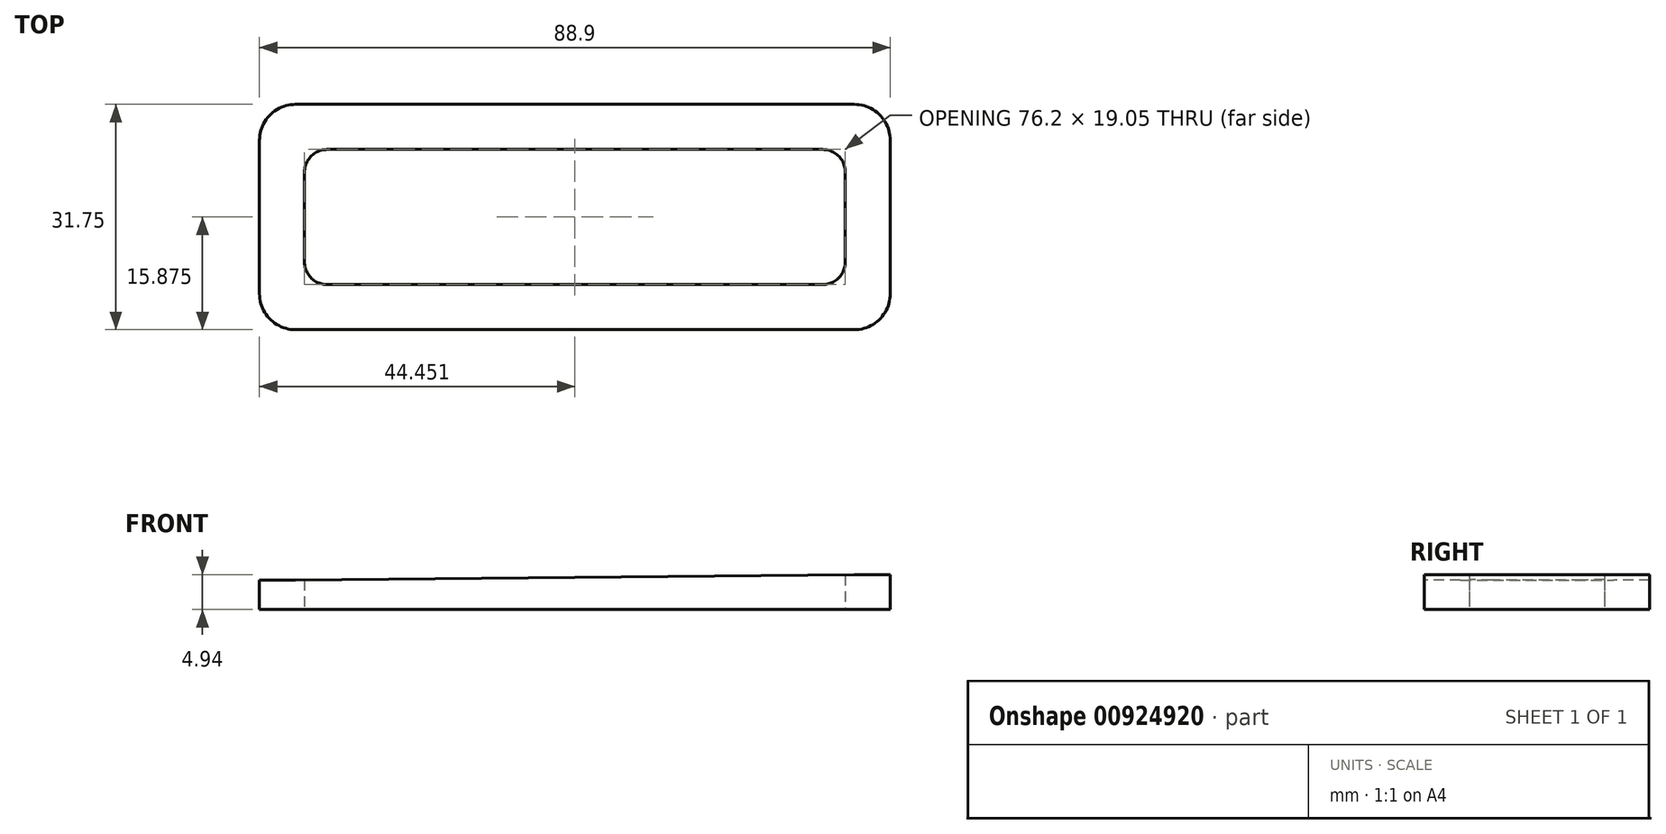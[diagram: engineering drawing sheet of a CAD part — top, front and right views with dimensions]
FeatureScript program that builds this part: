
annotation { "Feature Type Name" : "Feature", "Feature Type Description" : "" }
export const myFeature = defineFeature(function(context is Context, id is Id, definition is map)
    precondition{}
    {
        {
            var Q0;
            Q0=qCreatedBy(makeId("Front.planeOp"),FACE);
            var sketch = newSketch(context, id + "F0", { "sketchPlane" : qUnion([Q0])});
            skLineSegment(sketch, "E0", {"start": v(0, 0) * mm, "end": v(0, 2.39) * mm});
            skLineSegment(sketch, "E1", {"start": v(0, 2.39) * mm, "end": v(609.6, 7.95) * mm});
            skLineSegment(sketch, "E2", {"start": v(609.6, 7.95) * mm, "end": v(609.6, 0) * mm});
            skLineSegment(sketch, "E3", {"start": v(609.6, 0) * mm, "end": v(0, 0) * mm});
            skSolve(sketch);
        }
        {
            var Q0;
            Q0=qCreatedBy(makeId("Front.planeOp"),FACE);
            var sketch = newSketch(context, id + "F1", { "sketchPlane" : qUnion([Q0])});
            skLineSegment(sketch, "E4", {"start": v(609.6, 7.95) * mm, "end": v(520.7, 7.14) * mm});
            skLineSegment(sketch, "E5", {"start": v(520.7, 7.14) * mm, "end": v(520.7, 0) * mm});
            skLineSegment(sketch, "E6", {"start": v(520.7, 0) * mm, "end": v(609.6, 0) * mm});
            skLineSegment(sketch, "E7", {"start": v(609.6, 0) * mm, "end": v(609.6, 7.95) * mm});
            skSolve(sketch);
        }
        {
            var Q0;
            Q0=qCreatedBy(makeId("Front.planeOp"),FACE);
            var sketch = newSketch(context, id + "F2", { "sketchPlane" : qUnion([Q0])});
            skLineSegment(sketch, "E8", {"start": v(444.5, 6.44) * mm, "end": v(444.5, 0) * mm});
            skLineSegment(sketch, "E9", {"start": v(444.5, 0) * mm, "end": v(355.6, 0) * mm});
            skLineSegment(sketch, "E10", {"start": v(-261.65, 0) * mm, "end": v(-261.65, 0) * mm});
            skLineSegment(sketch, "E11", {"start": v(355.55, 5.63) * mm, "end": v(444.5, 6.44) * mm});
            skLineSegment(sketch, "E12", {"start": v(355.55, 5.63) * mm, "end": v(355.6, 0) * mm});
            skSolve(sketch);
        }
        {
            var Q0;
            Q0=makeQuery(id+"F0.imprint","IMPRINT",FACE,{"disambiguationData":[TD([[makeQuery(id+"F0.imprint","IMPRINT",EDGE,{"derivedFrom":sQuery(id+"F0.wireOp",EDGE,"E0")}),-1.0]])]});
            var sketch = newSketch(context, id + "F3", { "sketchPlane" : qUnion([Q0])});
            skLineSegment(sketch, "E13", {"start": v(279.35, 4.94) * mm, "end": v(279.35, 0) * mm});
            skLineSegment(sketch, "E14", {"start": v(279.35, 0) * mm, "end": v(190.45, 0) * mm});
            skLineSegment(sketch, "E15", {"start": v(190.45, 0) * mm, "end": v(190.45, 4.13) * mm});
            skLineSegment(sketch, "E16", {"start": v(190.45, 4.13) * mm, "end": v(279.35, 4.94) * mm});
            skSolve(sketch);
        }
        {
            var Q0;
            Q0=qSketchRegion(id+"F3",true);
            extrude(context, id + "F4", {"entities" : qUnion([Q0]), "depth" : 31.75 * mm, "offsetDistance" : 25.4 * mm});
        }
        {
            var Q0;
            Q0=makeQuery(id+"F4.opExtrude","SWEPT_FACE",FACE,{"disambiguationData":[OSD([sQuery(id+"F3.wireOp",EDGE,"E14")])]});
            var sketch = newSketch(context, id + "F5", { "sketchPlane" : qUnion([Q0])});
            skLineSegment(sketch, "E17.bottom", {"start": v(199.98, 25.4) * mm, "end": v(269.82, 25.4) * mm});
            skLineSegment(sketch, "E17.top", {"start": v(199.98, 6.35) * mm, "end": v(269.82, 6.35) * mm});
            skLineSegment(sketch, "E17.left", {"start": v(196.8, 22.22) * mm, "end": v(196.8, 9.52) * mm});
            skLineSegment(sketch, "E17.right", {"start": v(273, 22.23) * mm, "end": v(273, 9.53) * mm});
            skPoint(sketch, "E18.visualSharp", {"position": v(196.8, 25.4) * mm});
            skArc(sketch, "E18.filletArc", {"start": v(199.98, 25.4) * mm, "mid": v(197.73, 24.47) * mm, "end": v(196.8, 22.22) * mm});
            skPoint(sketch, "E19.visualSharp", {"position": v(273, 25.4) * mm});
            skArc(sketch, "E19.filletArc", {"start": v(273, 22.23) * mm, "mid": v(272.07, 24.47) * mm, "end": v(269.82, 25.4) * mm});
            skPoint(sketch, "E20.visualSharp", {"position": v(273, 6.35) * mm});
            skArc(sketch, "E20.filletArc", {"start": v(269.82, 6.35) * mm, "mid": v(272.07, 7.28) * mm, "end": v(273, 9.53) * mm});
            skPoint(sketch, "E21.visualSharp", {"position": v(196.8, 6.35) * mm});
            skArc(sketch, "E21.filletArc", {"start": v(196.8, 9.52) * mm, "mid": v(197.73, 7.28) * mm, "end": v(199.98, 6.35) * mm});
            skSolve(sketch);
        }
        {
            var Q0;
            Q0=makeQuery(id+"F5.imprint","IMPRINT",FACE,{"disambiguationData":[TD([[makeQuery(id+"F5.imprint","IMPRINT",EDGE,{"derivedFrom":sQuery(id+"F5.wireOp",EDGE,"E17.bottom")}),-1.0]])]});
            extrude(context, id + "F6", {"entities" : qUnion([Q0]), "operationType" : NewBodyOperationType.REMOVE, "endBound" : BoundingType.THROUGH_ALL, "oppositeDirection" : true, "depth" : 25.4 * mm, "offsetDistance" : 25.4 * mm});
        }
        {
            var Q0;
            Q0=makeQuery(id+"F4.opExtrude","CAP_EDGE",EDGE,{"disambiguationData":[OSD([sQuery(id+"F3.wireOp",EDGE,"E13")])],"isStart":false});
            var Q1;
            Q1=makeQuery(id+"F4.opExtrude","CAP_EDGE",EDGE,{"disambiguationData":[OSD([sQuery(id+"F3.wireOp",EDGE,"E15")])],"isStart":false});
            var Q2;
            Q2=makeQuery(id+"F4.opExtrude","CAP_EDGE",EDGE,{"disambiguationData":[OSD([sQuery(id+"F3.wireOp",EDGE,"E15")])],"isStart":true});
            var Q3;
            Q3=makeQuery(id+"F4.opExtrude","CAP_EDGE",EDGE,{"disambiguationData":[OSD([sQuery(id+"F3.wireOp",EDGE,"E13")])],"isStart":true});
            fillet(context, id + "F7", {"entities" : qUnion([Q0, Q1, Q2, Q3]), "radius" : 5.08 * mm, "tangentPropagation" : true, "allowEdgeOverflow" : false});
        }
    });
